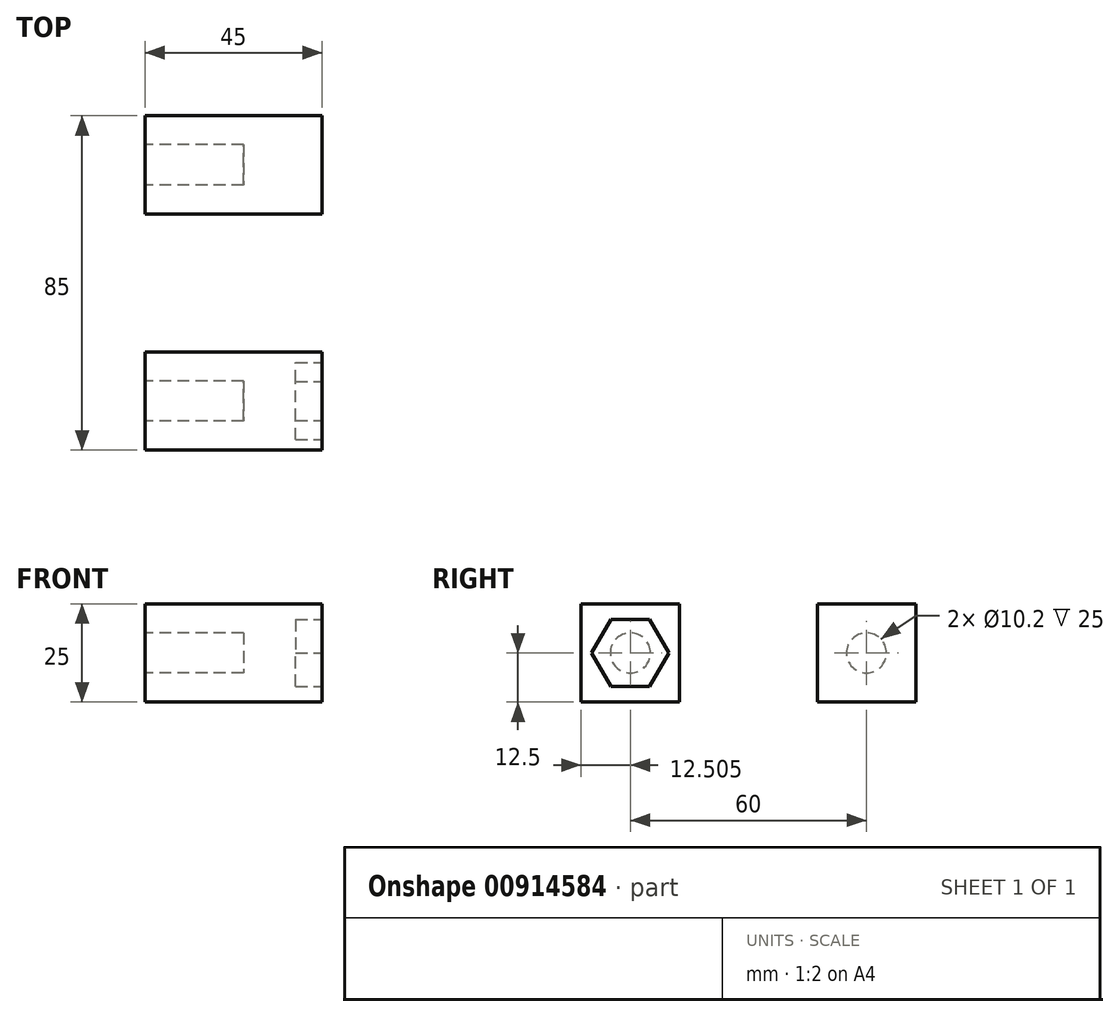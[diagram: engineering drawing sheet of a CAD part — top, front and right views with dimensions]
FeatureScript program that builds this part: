
annotation { "Feature Type Name" : "Feature", "Feature Type Description" : "" }
export const myFeature = defineFeature(function(context is Context, id is Id, definition is map)
    precondition{}
    {
        {
            var Q0;
            Q0=qCreatedBy(makeId("Top.planeOp"),FACE);
            var sketch = newSketch(context, id + "F0", { "sketchPlane" : qUnion([Q0])});
            skLineSegment(sketch, "E0.bottom", {"start": v(-10.06, 2) * mm, "end": v(34.94, 2) * mm});
            skLineSegment(sketch, "E0.top", {"start": v(-10.06, -23) * mm, "end": v(34.94, -23) * mm});
            skLineSegment(sketch, "E0.left", {"start": v(-10.06, 2) * mm, "end": v(-10.06, -23) * mm});
            skLineSegment(sketch, "E0.right", {"start": v(34.94, 2) * mm, "end": v(34.94, -23) * mm});
            skSolve(sketch);
        }
        {
            var Q0;
            Q0=makeQuery(id+"F0.imprint","IMPRINT",FACE,{"disambiguationData":[TD([[makeQuery(id+"F0.imprint","IMPRINT",EDGE,{"derivedFrom":sQuery(id+"F0.wireOp",EDGE,"E0.bottom")}),-1.0]])]});
            extrude(context, id + "F1", {"entities" : qUnion([Q0]), "depth" : 25 * mm, "offsetDistance" : 25 * mm});
        }
        {
            var Q0;
            Q0=makeQuery(id+"F1.opExtrude","SWEPT_FACE",FACE,{"disambiguationData":[OSD([sQuery(id+"F0.wireOp",EDGE,"E0.left")])]});
            var sketch = newSketch(context, id + "F2", { "sketchPlane" : qUnion([Q0])});
            skCircle(sketch, "E1", {"center": v(10.5, 12.5) * mm, "radius": 5.1 * mm});
            skLineSegment(sketch, "E2", {"start": v(23, 25) * mm, "end": v(-2, 0) * mm, "construction": true});
            skLineSegment(sketch, "E3", {"start": v(-2, 25) * mm, "end": v(23, 0) * mm, "construction": true});
            skSolve(sketch);
        }
        {
            var Q0;
            Q0=makeQuery(id+"F2.imprint","IMPRINT",FACE,{"disambiguationData":[TD([[makeQuery(id+"F2.imprint","IMPRINT",EDGE,{"derivedFrom":sQuery(id+"F2.wireOp",EDGE,"E1")}),1.0]])]});
            extrude(context, id + "F3", {"entities" : qUnion([Q0]), "operationType" : NewBodyOperationType.REMOVE, "oppositeDirection" : true, "depth" : 25 * mm, "offsetDistance" : 25 * mm});
        }
        {
            var Q0;
            Q0=makeQuery(id+"F1.opExtrude","SWEPT_BODY",BODY,{"disambiguationData":[OSD([sQuery(id+"F0.wireOp",EDGE,"E0.bottom"),sQuery(id+"F0.wireOp",EDGE,"E0.top"),sQuery(id+"F0.wireOp",EDGE,"E0.left"),sQuery(id+"F0.wireOp",EDGE,"E0.right")])]});
            transform(context, id + "F4", {"entities" : qUnion([Q0]), "transformType" : TransformType.TRANSLATION_3D, "dx" : 0 * mm, "dy" : 72 * mm, "dz" : 0 * mm, "makeCopy" : true});
        }
        {
            var Q0;
            Q0=makeQuery(id+"F1.opExtrude","SWEPT_FACE",FACE,{"disambiguationData":[OSD([sQuery(id+"F0.wireOp",EDGE,"E0.right")])]});
            var sketch = newSketch(context, id + "F5", { "sketchPlane" : qUnion([Q0])});
            skPoint(sketch, "E4.0", {"position": v(-10.5, 12.5) * mm});
            skCircle(sketch, "E5.cCircle", {"center": v(-10.5, 12.5) * mm, "radius": 8.5 * mm, "construction": true});
            skLineSegment(sketch, "E5.0", {"start": v(-5.6, 21) * mm, "end": v(-0.69, 12.5) * mm});
            skLineSegment(sketch, "E5.1", {"start": v(-0.69, 12.5) * mm, "end": v(-5.6, 4) * mm});
            skLineSegment(sketch, "E5.2", {"start": v(-5.6, 4) * mm, "end": v(-15.4, 4) * mm});
            skLineSegment(sketch, "E5.3", {"start": v(-15.4, 4) * mm, "end": v(-20.3, 12.5) * mm});
            skLineSegment(sketch, "E5.4", {"start": v(-20.3, 12.5) * mm, "end": v(-15.4, 21) * mm});
            skLineSegment(sketch, "E5.5", {"start": v(-15.4, 21) * mm, "end": v(-5.6, 21) * mm});
            skPoint(sketch, "E5.0.midPoint", {"position": v(-3.14, 16.75) * mm});
            skSolve(sketch);
        }
        {
            var Q0;
            Q0=makeQuery(id+"F4.opPattern","COPY",BODY,{"derivedFrom":makeQuery(id+"F1.opExtrude","SWEPT_BODY",BODY,{"disambiguationData":[OSD([sQuery(id+"F0.wireOp",EDGE,"E0.bottom"),sQuery(id+"F0.wireOp",EDGE,"E0.top"),sQuery(id+"F0.wireOp",EDGE,"E0.left"),sQuery(id+"F0.wireOp",EDGE,"E0.right")])]}),"instanceName":"1"});
            deleteBodies(context, id + "F6", {"entities" : qUnion([Q0])});
        }
        {
            var Q0;
            Q0=makeQuery(id+"F1.opExtrude","SWEPT_BODY",BODY,{"disambiguationData":[OSD([sQuery(id+"F0.wireOp",EDGE,"E0.bottom"),sQuery(id+"F0.wireOp",EDGE,"E0.top"),sQuery(id+"F0.wireOp",EDGE,"E0.left"),sQuery(id+"F0.wireOp",EDGE,"E0.right")])]});
            transform(context, id + "F7", {"entities" : qUnion([Q0]), "transformType" : TransformType.TRANSLATION_3D, "dx" : 0 * mm, "dy" : 60 * mm, "dz" : 0 * mm, "makeCopy" : true});
        }
        {
            var Q0;
            Q0=makeQuery(id+"F5.imprint","IMPRINT",FACE,{"disambiguationData":[TD([[makeQuery(id+"F5.imprint","IMPRINT",EDGE,{"derivedFrom":sQuery(id+"F5.wireOp",EDGE,"E5.0")}),-1.0]])]});
            extrude(context, id + "F8", {"entities" : qUnion([Q0]), "operationType" : NewBodyOperationType.REMOVE, "oppositeDirection" : true, "depth" : 6.8 * mm, "offsetDistance" : 25 * mm});
        }
        {
            var Q0;
            Q0=makeQuery(id+"F1.opExtrude","SWEPT_BODY",BODY,{"disambiguationData":[OSD([sQuery(id+"F0.wireOp",EDGE,"E0.bottom"),sQuery(id+"F0.wireOp",EDGE,"E0.top"),sQuery(id+"F0.wireOp",EDGE,"E0.left"),sQuery(id+"F0.wireOp",EDGE,"E0.right")])]});
            transform(context, id + "F9", {"entities" : qUnion([Q0]), "transformType" : TransformType.TRANSLATION_3D, "dx" : 0 * mm, "dy" : -50 * mm, "dz" : 0 * mm, "makeCopy" : true});
        }
        {
            var Q0;
            Q0=makeQuery(id+"F9.opPattern","COPY",BODY,{"derivedFrom":makeQuery(id+"F1.opExtrude","SWEPT_BODY",BODY,{"disambiguationData":[OSD([sQuery(id+"F0.wireOp",EDGE,"E0.bottom"),sQuery(id+"F0.wireOp",EDGE,"E0.top"),sQuery(id+"F0.wireOp",EDGE,"E0.left"),sQuery(id+"F0.wireOp",EDGE,"E0.right")])]}),"instanceName":"1"});
            deleteBodies(context, id + "F10", {"entities" : qUnion([Q0])});
        }
    });
